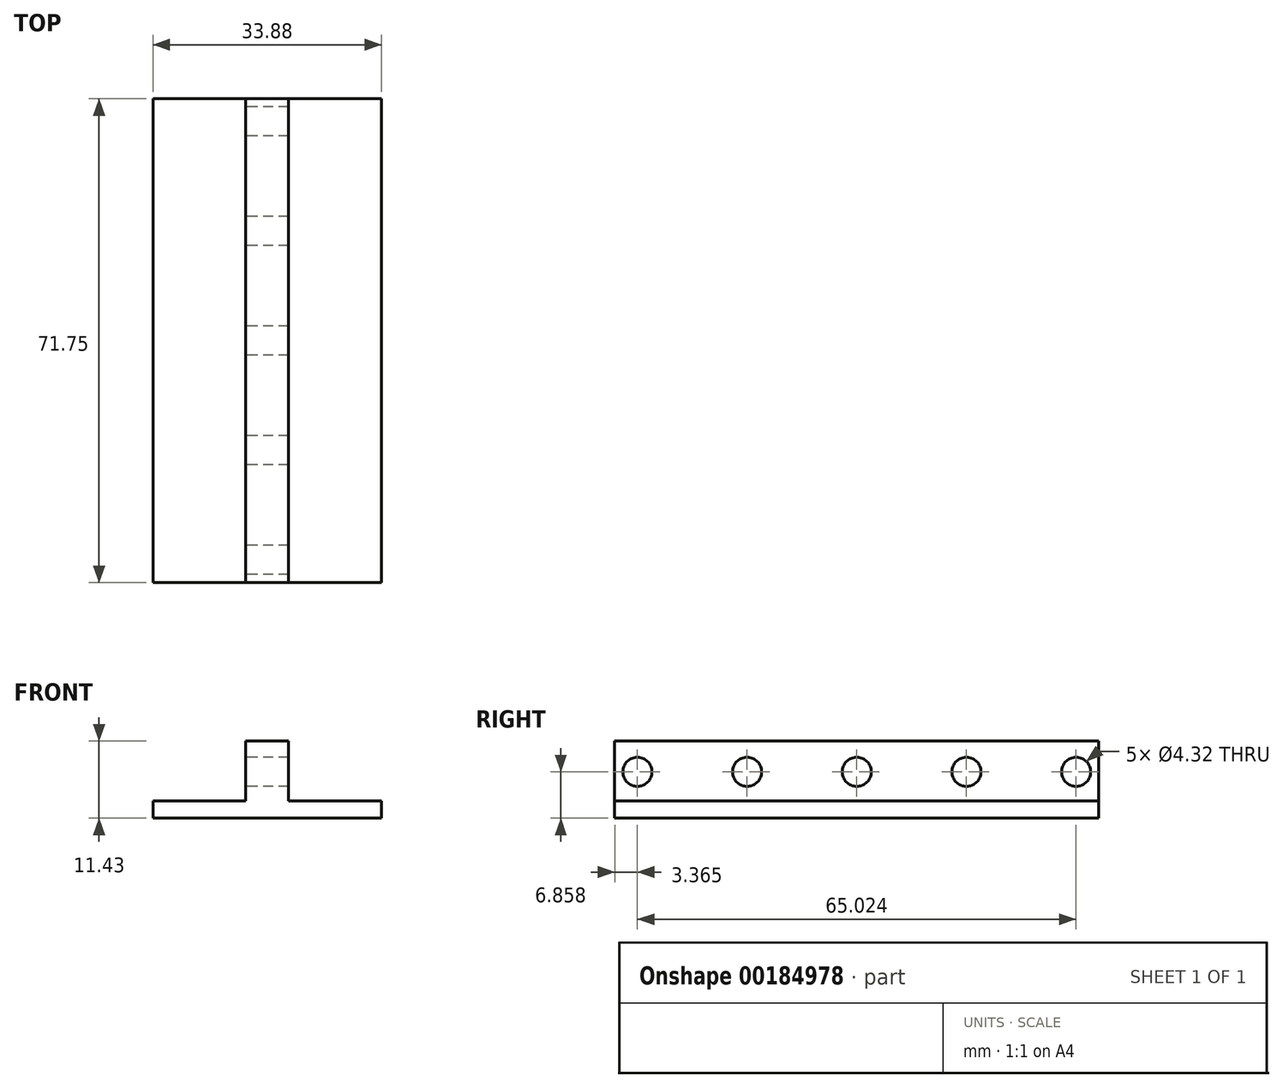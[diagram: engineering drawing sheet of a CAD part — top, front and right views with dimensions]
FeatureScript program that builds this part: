
annotation { "Feature Type Name" : "Feature", "Feature Type Description" : "" }
export const myFeature = defineFeature(function(context is Context, id is Id, definition is map)
    precondition{}
    {
        {
            var Q0;
            Q0=qCreatedBy(makeId("Top.planeOp"),FACE);
            var sketch = newSketch(context, id + "F0", { "sketchPlane" : qUnion([Q0])});
            skLineSegment(sketch, "E0.bottom", {"start": v(-33.88, 37.83) * mm, "end": v(0, 37.83) * mm});
            skLineSegment(sketch, "E0.top", {"start": v(-33.88, -33.92) * mm, "end": v(0, -33.92) * mm});
            skLineSegment(sketch, "E0.left", {"start": v(-33.88, 37.83) * mm, "end": v(-33.88, -33.92) * mm});
            skLineSegment(sketch, "E0.right", {"start": v(0, 37.83) * mm, "end": v(0, -33.92) * mm});
            skSolve(sketch);
        }
        {
            var Q0;
            Q0=makeQuery(id+"F0.imprint","IMPRINT",FACE,{"disambiguationData":[TD([[makeQuery(id+"F0.imprint","IMPRINT",EDGE,{"derivedFrom":sQuery(id+"F0.wireOp",EDGE,"E0.bottom")}),-1.0]])]});
            extrude(context, id + "F1", {"entities" : qUnion([Q0]), "depth" : 2.54 * mm});
        }
        {
            var Q0;
            Q0=makeQuery(id+"F1.opExtrude","CAP_FACE",FACE,{"disambiguationData":[OSD([sQuery(id+"F0.wireOp",EDGE,"E0.bottom"),sQuery(id+"F0.wireOp",EDGE,"E0.top"),sQuery(id+"F0.wireOp",EDGE,"E0.left"),sQuery(id+"F0.wireOp",EDGE,"E0.right")])],"isStart":false});
            var sketch = newSketch(context, id + "F2", { "sketchPlane" : qUnion([Q0])});
            skLineSegment(sketch, "E1.bottom", {"start": v(-20.12, 37.83) * mm, "end": v(-13.77, 37.83) * mm});
            skLineSegment(sketch, "E1.top", {"start": v(-20.12, -33.92) * mm, "end": v(-13.77, -33.92) * mm});
            skLineSegment(sketch, "E1.left", {"start": v(-20.12, 37.83) * mm, "end": v(-20.12, -33.92) * mm});
            skLineSegment(sketch, "E1.right", {"start": v(-13.77, 37.83) * mm, "end": v(-13.77, -33.92) * mm});
            skSolve(sketch);
        }
        {
            var Q0;
            Q0=makeQuery(id+"F2.imprint","IMPRINT",FACE,{"disambiguationData":[TD([[makeQuery(id+"F2.imprint","IMPRINT",EDGE,{"derivedFrom":sQuery(id+"F2.wireOp",EDGE,"E1.bottom")}),-1.0]])]});
            extrude(context, id + "F3", {"entities" : qUnion([Q0]), "operationType" : NewBodyOperationType.ADD, "depth" : 8.9 * mm});
        }
        {
            var Q0;
            Q0=makeQuery(id+"F3.opExtrude","SWEPT_FACE",FACE,{"disambiguationData":[OSD([sQuery(id+"F2.wireOp",EDGE,"E1.left")])]});
            var sketch = newSketch(context, id + "F4", { "sketchPlane" : qUnion([Q0])});
            skCircle(sketch, "E2", {"center": v(-34.47, 6.86) * mm, "radius": 2.16 * mm});
            skCircle(sketch, "E3", {"center": v(-18.21, 6.86) * mm, "radius": 2.16 * mm});
            skCircle(sketch, "E4", {"center": v(-1.96, 6.86) * mm, "radius": 2.16 * mm});
            skCircle(sketch, "E5", {"center": v(14.3, 6.86) * mm, "radius": 2.16 * mm});
            skCircle(sketch, "E6", {"center": v(30.56, 6.86) * mm, "radius": 2.16 * mm});
            skSolve(sketch);
        }
        {
            var Q0;
            Q0=makeQuery(id+"F4.imprint","IMPRINT",FACE,{"disambiguationData":[TD([[makeQuery(id+"F4.imprint","IMPRINT",EDGE,{"derivedFrom":sQuery(id+"F4.wireOp",EDGE,"E3")}),1.0]])]});
            var Q1;
            Q1=makeQuery(id+"F4.imprint","IMPRINT",FACE,{"disambiguationData":[TD([[makeQuery(id+"F4.imprint","IMPRINT",EDGE,{"derivedFrom":sQuery(id+"F4.wireOp",EDGE,"E2")}),1.0]])]});
            var Q2;
            Q2=makeQuery(id+"F4.imprint","IMPRINT",FACE,{"disambiguationData":[TD([[makeQuery(id+"F4.imprint","IMPRINT",EDGE,{"derivedFrom":sQuery(id+"F4.wireOp",EDGE,"E4")}),1.0]])]});
            var Q3;
            Q3=makeQuery(id+"F4.imprint","IMPRINT",FACE,{"disambiguationData":[TD([[makeQuery(id+"F4.imprint","IMPRINT",EDGE,{"derivedFrom":sQuery(id+"F4.wireOp",EDGE,"E5")}),1.0]])]});
            var Q4;
            Q4=makeQuery(id+"F4.imprint","IMPRINT",FACE,{"disambiguationData":[TD([[makeQuery(id+"F4.imprint","IMPRINT",EDGE,{"derivedFrom":sQuery(id+"F4.wireOp",EDGE,"E6")}),1.0]])]});
            extrude(context, id + "F5", {"entities" : qUnion([Q0, Q1, Q2, Q3, Q4]), "operationType" : NewBodyOperationType.REMOVE, "oppositeDirection" : true, "depth" : 6.35 * mm});
        }
    });
